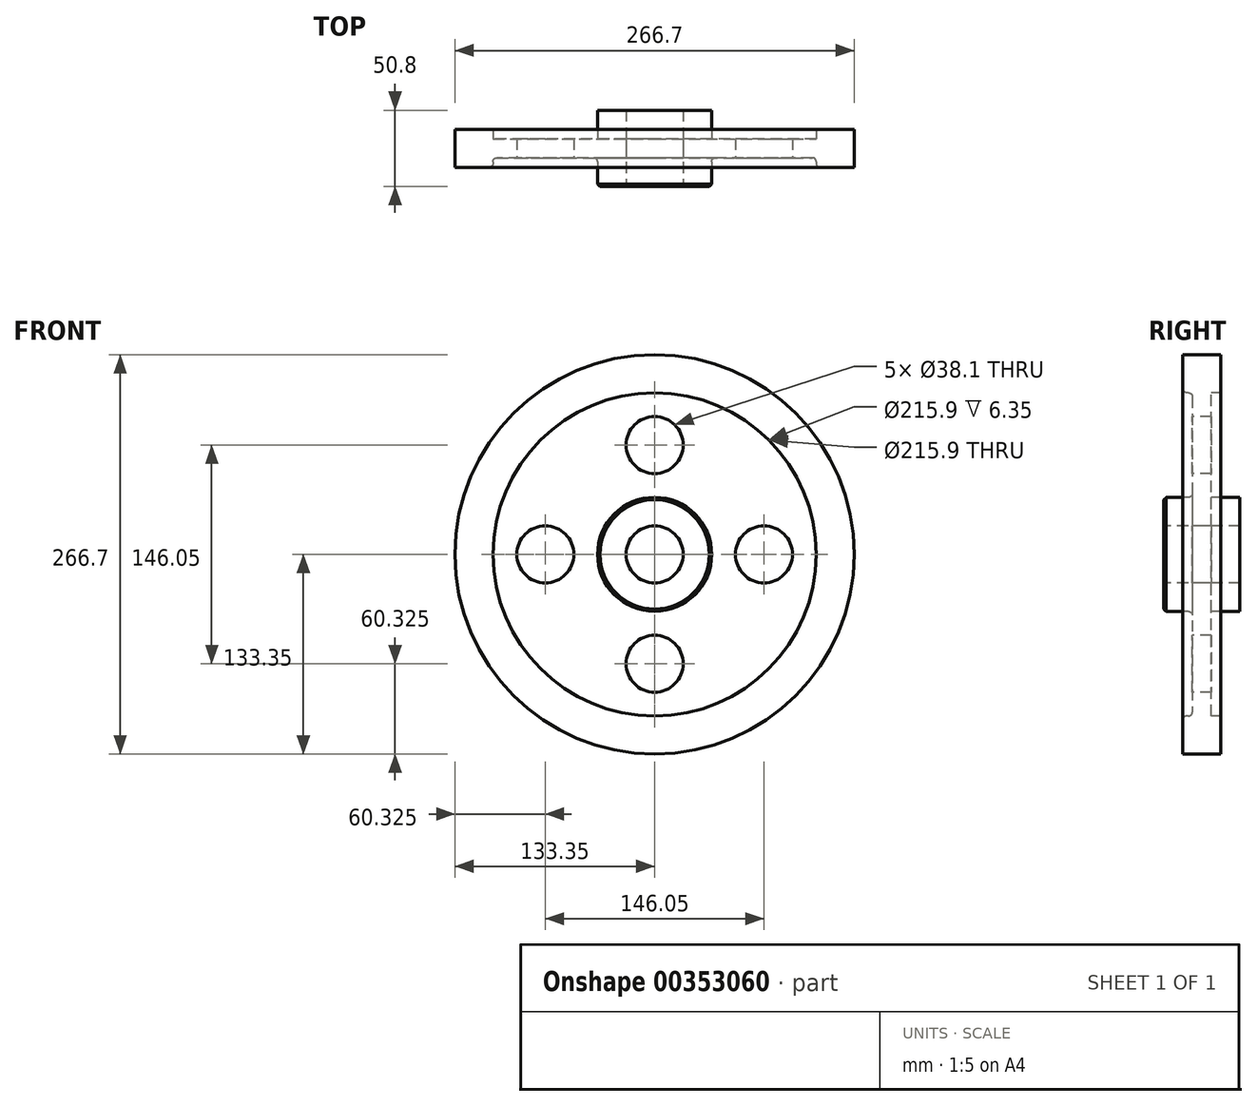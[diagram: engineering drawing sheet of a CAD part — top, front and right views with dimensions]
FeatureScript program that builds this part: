
annotation { "Feature Type Name" : "Feature", "Feature Type Description" : "" }
export const myFeature = defineFeature(function(context is Context, id is Id, definition is map)
    precondition{}
    {
        {
            var Q0;
            Q0=qCreatedBy(makeId("Right.planeOp"),FACE);
            var sketch = newSketch(context, id + "F0", { "sketchPlane" : qUnion([Q0])});
            skLineSegment(sketch, "E0", {"start": v(0, 0) * mm, "end": v(75.6, 0) * mm, "construction": true});
            skLineSegment(sketch, "E1.0", {"start": v(0, -2432.05) * mm, "end": v(75.6, -2432.05) * mm, "construction": true});
            skLineSegment(sketch, "E2.0", {"start": v(6.35, 107.95) * mm, "end": v(12.7, 107.95) * mm});
            skLineSegment(sketch, "E3", {"start": v(0, 133.35) * mm, "end": v(0, 0) * mm, "construction": true});
            skLineSegment(sketch, "E4.0", {"start": v(12.7, 133.35) * mm, "end": v(12.7, 107.95) * mm});
            skLineSegment(sketch, "E5.0", {"start": v(6.35, 107.95) * mm, "end": v(6.35, 38.1) * mm});
            skLineSegment(sketch, "E6", {"start": v(0, 133.35) * mm, "end": v(12.7, 133.35) * mm});
            skLineSegment(sketch, "E7.0", {"start": v(0, 317.5) * mm, "end": v(75.6, 317.5) * mm});
            skLineSegment(sketch, "E8.0", {"start": v(0, 38.1) * mm, "end": v(25.4, 38.1) * mm});
            skLineSegment(sketch, "E9.MirrorCS", {"start": v(0, 133.35) * mm, "end": v(-12.7, 133.35) * mm});
            skLineSegment(sketch, "E10.MirrorCS", {"start": v(-12.7, 133.35) * mm, "end": v(-12.7, 107.95) * mm});
            skLineSegment(sketch, "E11.MirrorCS", {"start": v(-6.35, 107.95) * mm, "end": v(-12.7, 107.95) * mm});
            skLineSegment(sketch, "E12.MirrorCS", {"start": v(-6.35, 107.95) * mm, "end": v(-6.35, 38.1) * mm});
            skLineSegment(sketch, "E13.MirrorCS", {"start": v(0, 38.1) * mm, "end": v(-25.4, 38.1) * mm});
            skLineSegment(sketch, "E14.0", {"start": v(0, 19.05) * mm, "end": v(75.6, 19.05) * mm});
            skLineSegment(sketch, "E15.bottom", {"start": v(-25.4, 38.1) * mm, "end": v(25.4, 38.1) * mm});
            skLineSegment(sketch, "E15.top", {"start": v(-25.4, 19.05) * mm, "end": v(25.4, 19.05) * mm});
            skLineSegment(sketch, "E15.left", {"start": v(-25.4, 38.1) * mm, "end": v(-25.4, 19.05) * mm});
            skLineSegment(sketch, "E15.right", {"start": v(25.4, 38.1) * mm, "end": v(25.4, 19.05) * mm});
            skPoint(sketch, "E16.MirrorCS.end.orphan", {"position": v(-25.4, 57.15) * mm});
            skPoint(sketch, "E16.MirrorCS.start.orphan", {"position": v(-6.35, 57.15) * mm});
            skPoint(sketch, "E17.trimOffspring.start.orphan", {"position": v(25.4, 57.15) * mm});
            skPoint(sketch, "E18.orphan", {"position": v(6.35, 57.15) * mm});
            skSolve(sketch);
        }
        {
            var Q0;
            Q0=makeQuery(id+"F0.imprint","IMPRINT",FACE,{"disambiguationData":[TD([[makeQuery(id+"F0.imprint","IMPRINT",EDGE,{"derivedFrom":sQuery(id+"F0.wireOp",EDGE,"E2.0")}),1.0]])]});
            var Q1;
            {var subQ2=sQuery(id+"F0.wireOp",EDGE,"E15.left");Q1=makeQuery(id+"F0.imprint","IMPRINT",FACE,{"disambiguationData":[TD([[makeQuery(id+"F0.imprint","IMPRINT",EDGE,{"derivedFrom":subQ2}),1.0]])]});}
            var Q2;
            Q2=sQuery(id+"F0.wireOp",EDGE,"E0");
            revolve(context, id + "F1", {"entities" : qUnion([Q0, Q1]), "axis" : qUnion([Q2]), "revolveType" : RevolveType.FULL});
        }
        {
            var Q0;
            Q0=makeQuery(id+"F1.opRevolve","SWEPT_FACE",FACE,{"disambiguationData":[OSD([sQuery(id+"F0.wireOp",EDGE,"E12.MirrorCS")])]});
            var sketch = newSketch(context, id + "F2", { "sketchPlane" : qUnion([Q0])});
            skLineSegment(sketch, "E19", {"start": v(0, 0) * mm, "end": v(0, 73.03) * mm});
            skCircle(sketch, "E20", {"center": v(0, 73.03) * mm, "radius": 19.05 * mm});
            skCircle(sketch, "E21.1.0", {"center": v(-73.03, 0) * mm, "radius": 19.05 * mm});
            skCircle(sketch, "E21.2.0", {"center": v(0, -73.03) * mm, "radius": 19.05 * mm});
            skCircle(sketch, "E21.3.0", {"center": v(73.03, 0) * mm, "radius": 19.05 * mm});
            skPoint(sketch, "E21.center", {"position": v(0, 0) * mm});
            skSolve(sketch);
        }
        {
            var Q0;
            {var subQ0=sQuery(id+"F2.wireOp",EDGE,"E21.3.0");var subQ1=makeQuery(id+"F1.opRevolve","SWEPT_EDGE",EDGE,{"disambiguationData":[OSD([sQuery(id+"F0.wireOp",EDGE,"E12.MirrorCS"),sQuery(id+"F0.wireOp",EDGE,"E16.MirrorCS")])]});var subQ2=makeQuery(id+"F2.imprint","INTERSECT",VERTEX,{"disambiguationData":[OD(0.0)],"derivedFrom":[subQ1,subQ0]});Q0=makeQuery(id+"F2.imprint","IMPRINT",FACE,{"disambiguationData":[TD([[makeQuery(id+"F2.imprint","IMPRINT",EDGE,{"disambiguationData":[TD([[subQ2,1.0]])],"derivedFrom":subQ0}),1.0]])]});}
            var Q1;
            {var subQ0=sQuery(id+"F2.wireOp",EDGE,"E21.2.0");var subQ1=makeQuery(id+"F1.opRevolve","SWEPT_EDGE",EDGE,{"disambiguationData":[OSD([sQuery(id+"F0.wireOp",EDGE,"E12.MirrorCS"),sQuery(id+"F0.wireOp",EDGE,"E16.MirrorCS")])]});var subQ2=makeQuery(id+"F2.imprint","INTERSECT",VERTEX,{"disambiguationData":[OD(0.0)],"derivedFrom":[subQ1,subQ0]});Q1=makeQuery(id+"F2.imprint","IMPRINT",FACE,{"disambiguationData":[TD([[makeQuery(id+"F2.imprint","IMPRINT",EDGE,{"disambiguationData":[TD([[subQ2,-1.0]])],"derivedFrom":subQ0}),1.0]])]});}
            var Q2;
            {var subQ0=sQuery(id+"F2.wireOp",EDGE,"E21.1.0");var subQ1=makeQuery(id+"F1.opRevolve","SWEPT_EDGE",EDGE,{"disambiguationData":[OSD([sQuery(id+"F0.wireOp",EDGE,"E12.MirrorCS"),sQuery(id+"F0.wireOp",EDGE,"E16.MirrorCS")])]});var subQ2=makeQuery(id+"F2.imprint","INTERSECT",VERTEX,{"disambiguationData":[OD(0.0)],"derivedFrom":[subQ1,subQ0]});Q2=makeQuery(id+"F2.imprint","IMPRINT",FACE,{"disambiguationData":[TD([[makeQuery(id+"F2.imprint","IMPRINT",EDGE,{"disambiguationData":[TD([[subQ2,-1.0]])],"derivedFrom":subQ0}),1.0]])]});}
            var Q3;
            {var subQ0=sQuery(id+"F2.wireOp",EDGE,"E20");var subQ1=makeQuery(id+"F1.opRevolve","SWEPT_EDGE",EDGE,{"disambiguationData":[OSD([sQuery(id+"F0.wireOp",EDGE,"E12.MirrorCS"),sQuery(id+"F0.wireOp",EDGE,"E16.MirrorCS")])]});var subQ2=makeQuery(id+"F2.imprint","INTERSECT",VERTEX,{"disambiguationData":[OD(0.0)],"derivedFrom":[subQ1,subQ0]});Q3=makeQuery(id+"F2.imprint","IMPRINT",FACE,{"disambiguationData":[TD([[makeQuery(id+"F2.imprint","IMPRINT",EDGE,{"disambiguationData":[TD([[subQ2,1.0]])],"derivedFrom":subQ0}),1.0]])]});}
            var Q4;
            Q4=makeQuery(id+"F2.imprint","IMPRINT",FACE,{"disambiguationData":[TD([[makeQuery(id+"F2.imprint","IMPRINT",EDGE,{"derivedFrom":sQuery(id+"F2.wireOp",EDGE,"E21.1.0")}),1.0]])]});
            var Q5;
            Q5=makeQuery(id+"F2.imprint","IMPRINT",FACE,{"disambiguationData":[TD([[makeQuery(id+"F2.imprint","IMPRINT",EDGE,{"derivedFrom":sQuery(id+"F2.wireOp",EDGE,"E21.3.0")}),1.0]])]});
            var Q6;
            Q6=makeQuery(id+"F2.imprint","IMPRINT",FACE,{"disambiguationData":[TD([[makeQuery(id+"F2.imprint","IMPRINT",EDGE,{"derivedFrom":sQuery(id+"F2.wireOp",EDGE,"E20")}),1.0]])]});
            var Q7;
            Q7=makeQuery(id+"F2.imprint","IMPRINT",FACE,{"disambiguationData":[TD([[makeQuery(id+"F2.imprint","IMPRINT",EDGE,{"derivedFrom":sQuery(id+"F2.wireOp",EDGE,"E21.2.0")}),1.0]])]});
            extrude(context, id + "F3", {"entities" : qUnion([Q0, Q1, Q2, Q3, Q4, Q5, Q6, Q7]), "operationType" : NewBodyOperationType.REMOVE, "oppositeDirection" : true, "depth" : 25.4 * mm});
        }
        {
            var Q0;
            {var subQ0=sQuery(id+"F2.wireOp",EDGE,"E20");var subQ1=sQuery(id+"F0.wireOp",EDGE,"E12.MirrorCS");var subQ2=sQuery(id+"F0.wireOp",EDGE,"E16.MirrorCS");var subQ3=sQuery(id+"F2.wireOp",EDGE,"E21.3.0");var subQ4=makeQuery(id+"F1.opRevolve","SWEPT_EDGE",EDGE,{"disambiguationData":[OSD([subQ1,subQ2])]});var subQ5=makeQuery(id+"F2.imprint","INTERSECT",VERTEX,{"derivedFrom":[subQ4,sQuery(id+"F2.wireOp",EDGE,"E19")]});var subQ6=sQuery(id+"F2.wireOp",EDGE,"E21.1.0");var subQ7=sQuery(id+"F2.wireOp",EDGE,"E21.2.0");Q0=makeQuery(id+"F3.boolean.opBoolean","SPLIT",EDGE,{"disambiguationData":[TD([makeQuery(id+"F1.opRevolve","SWEPT_FACE",FACE,{"disambiguationData":[OSD([sQuery(id+"F0.wireOp",EDGE,"4109ed80-6467-4f52-9944-9ac0837b3c0b.0")])]}),makeQuery(id+"F1.opRevolve","SWEPT_FACE",FACE,{"disambiguationData":[OSD([subQ1])]}),makeQuery(id+"F1.opRevolve","SWEPT_FACE",FACE,{"disambiguationData":[OSD([subQ2])]}),makeQuery(id+"F3.opExtrude","SWEPT_FACE",FACE,{"disambiguationData":[OSD([subQ0])]}),makeQuery(id+"F3.opExtrude","SWEPT_FACE",FACE,{"disambiguationData":[OSD([subQ3])]}),makeQuery(id+"F3.opExtrude","SWEPT_FACE",FACE,{"disambiguationData":[OSD([subQ1,subQ2]),TDD([makeQuery(id+"F2.imprint","IMPRINT",EDGE,{"disambiguationData":[TD([[subQ5,-1.0]])],"derivedFrom":subQ4}),makeQuery(id+"F2.imprint","IMPRINT",EDGE,{"disambiguationData":[TD([[subQ5,1.0]])],"derivedFrom":subQ4})])]}),makeQuery(id+"F3.opExtrude","SWEPT_FACE",FACE,{"disambiguationData":[OSD([subQ1,subQ2]),TDD([makeQuery(id+"F2.imprint","IMPRINT",EDGE,{"disambiguationData":[TD([[makeQuery(id+"F2.imprint","INTERSECT",VERTEX,{"disambiguationData":[OD(0.0)],"derivedFrom":[subQ4,subQ6]}),-1.0]])],"derivedFrom":subQ4})])]}),makeQuery(id+"F3.opExtrude","SWEPT_FACE",FACE,{"disambiguationData":[OSD([subQ1,subQ2]),TDD([makeQuery(id+"F2.imprint","IMPRINT",EDGE,{"disambiguationData":[TD([[makeQuery(id+"F2.imprint","INTERSECT",VERTEX,{"disambiguationData":[OD(0.0)],"derivedFrom":[subQ4,subQ7]}),-1.0]])],"derivedFrom":subQ4})])]}),makeQuery(id+"F3.opExtrude","SWEPT_FACE",FACE,{"disambiguationData":[OSD([subQ1,subQ2]),TDD([makeQuery(id+"F2.imprint","IMPRINT",EDGE,{"disambiguationData":[TD([[makeQuery(id+"F2.imprint","INTERSECT",VERTEX,{"disambiguationData":[OD(0.0)],"derivedFrom":[subQ4,subQ3]}),1.0]])],"derivedFrom":subQ4})])]})])],"derivedFrom":subQ4});}
            var Q1;
            {var subQ0=sQuery(id+"F2.wireOp",EDGE,"E20");var subQ1=sQuery(id+"F0.wireOp",EDGE,"E12.MirrorCS");var subQ2=sQuery(id+"F0.wireOp",EDGE,"E16.MirrorCS");var subQ3=sQuery(id+"F2.wireOp",EDGE,"E21.1.0");var subQ4=sQuery(id+"F2.wireOp",EDGE,"E21.2.0");var subQ5=makeQuery(id+"F1.opRevolve","SWEPT_EDGE",EDGE,{"disambiguationData":[OSD([subQ1,subQ2])]});var subQ6=makeQuery(id+"F2.imprint","INTERSECT",VERTEX,{"derivedFrom":[subQ5,sQuery(id+"F2.wireOp",EDGE,"E19")]});var subQ7=sQuery(id+"F2.wireOp",EDGE,"E21.3.0");Q1=makeQuery(id+"F3.boolean.opBoolean","SPLIT",EDGE,{"disambiguationData":[TD([makeQuery(id+"F1.opRevolve","SWEPT_FACE",FACE,{"disambiguationData":[OSD([sQuery(id+"F0.wireOp",EDGE,"4109ed80-6467-4f52-9944-9ac0837b3c0b.0")])]}),makeQuery(id+"F1.opRevolve","SWEPT_FACE",FACE,{"disambiguationData":[OSD([subQ1])]}),makeQuery(id+"F1.opRevolve","SWEPT_FACE",FACE,{"disambiguationData":[OSD([subQ2])]}),makeQuery(id+"F3.opExtrude","SWEPT_FACE",FACE,{"disambiguationData":[OSD([subQ0])]}),makeQuery(id+"F3.opExtrude","SWEPT_FACE",FACE,{"disambiguationData":[OSD([subQ3])]}),makeQuery(id+"F3.opExtrude","SWEPT_FACE",FACE,{"disambiguationData":[OSD([subQ1,subQ2]),TDD([makeQuery(id+"F2.imprint","IMPRINT",EDGE,{"disambiguationData":[TD([[subQ6,-1.0]])],"derivedFrom":subQ5}),makeQuery(id+"F2.imprint","IMPRINT",EDGE,{"disambiguationData":[TD([[subQ6,1.0]])],"derivedFrom":subQ5})])]}),makeQuery(id+"F3.opExtrude","SWEPT_FACE",FACE,{"disambiguationData":[OSD([subQ1,subQ2]),TDD([makeQuery(id+"F2.imprint","IMPRINT",EDGE,{"disambiguationData":[TD([[makeQuery(id+"F2.imprint","INTERSECT",VERTEX,{"disambiguationData":[OD(0.0)],"derivedFrom":[subQ5,subQ3]}),-1.0]])],"derivedFrom":subQ5})])]}),makeQuery(id+"F3.opExtrude","SWEPT_FACE",FACE,{"disambiguationData":[OSD([subQ1,subQ2]),TDD([makeQuery(id+"F2.imprint","IMPRINT",EDGE,{"disambiguationData":[TD([[makeQuery(id+"F2.imprint","INTERSECT",VERTEX,{"disambiguationData":[OD(0.0)],"derivedFrom":[subQ5,subQ4]}),-1.0]])],"derivedFrom":subQ5})])]}),makeQuery(id+"F3.opExtrude","SWEPT_FACE",FACE,{"disambiguationData":[OSD([subQ1,subQ2]),TDD([makeQuery(id+"F2.imprint","IMPRINT",EDGE,{"disambiguationData":[TD([[makeQuery(id+"F2.imprint","INTERSECT",VERTEX,{"disambiguationData":[OD(0.0)],"derivedFrom":[subQ5,subQ7]}),1.0]])],"derivedFrom":subQ5})])]})])],"derivedFrom":subQ5});}
            var Q2;
            {var subQ0=sQuery(id+"F2.wireOp",EDGE,"E21.2.0");var subQ1=sQuery(id+"F0.wireOp",EDGE,"E12.MirrorCS");var subQ2=sQuery(id+"F0.wireOp",EDGE,"E16.MirrorCS");var subQ3=sQuery(id+"F2.wireOp",EDGE,"E21.3.0");var subQ4=makeQuery(id+"F1.opRevolve","SWEPT_EDGE",EDGE,{"disambiguationData":[OSD([subQ1,subQ2])]});var subQ5=makeQuery(id+"F2.imprint","INTERSECT",VERTEX,{"derivedFrom":[subQ4,sQuery(id+"F2.wireOp",EDGE,"E19")]});var subQ7=sQuery(id+"F2.wireOp",EDGE,"E21.1.0");Q2=makeQuery(id+"F3.boolean.opBoolean","SPLIT",EDGE,{"disambiguationData":[TD([makeQuery(id+"F1.opRevolve","SWEPT_FACE",FACE,{"disambiguationData":[OSD([sQuery(id+"F0.wireOp",EDGE,"4109ed80-6467-4f52-9944-9ac0837b3c0b.0")])]}),makeQuery(id+"F1.opRevolve","SWEPT_FACE",FACE,{"disambiguationData":[OSD([subQ1])]}),makeQuery(id+"F1.opRevolve","SWEPT_FACE",FACE,{"disambiguationData":[OSD([subQ2])]}),makeQuery(id+"F3.opExtrude","SWEPT_FACE",FACE,{"disambiguationData":[OSD([subQ0])]}),makeQuery(id+"F3.opExtrude","SWEPT_FACE",FACE,{"disambiguationData":[OSD([subQ3])]}),makeQuery(id+"F3.opExtrude","SWEPT_FACE",FACE,{"disambiguationData":[OSD([subQ1,subQ2]),TDD([makeQuery(id+"F2.imprint","IMPRINT",EDGE,{"disambiguationData":[TD([[subQ5,-1.0]])],"derivedFrom":subQ4}),makeQuery(id+"F2.imprint","IMPRINT",EDGE,{"disambiguationData":[TD([[subQ5,1.0]])],"derivedFrom":subQ4})])]}),makeQuery(id+"F3.opExtrude","SWEPT_FACE",FACE,{"disambiguationData":[OSD([subQ1,subQ2]),TDD([makeQuery(id+"F2.imprint","IMPRINT",EDGE,{"disambiguationData":[TD([[makeQuery(id+"F2.imprint","INTERSECT",VERTEX,{"disambiguationData":[OD(0.0)],"derivedFrom":[subQ4,subQ7]}),-1.0]])],"derivedFrom":subQ4})])]}),makeQuery(id+"F3.opExtrude","SWEPT_FACE",FACE,{"disambiguationData":[OSD([subQ1,subQ2]),TDD([makeQuery(id+"F2.imprint","IMPRINT",EDGE,{"disambiguationData":[TD([[makeQuery(id+"F2.imprint","INTERSECT",VERTEX,{"disambiguationData":[OD(0.0)],"derivedFrom":[subQ4,subQ0]}),-1.0]])],"derivedFrom":subQ4})])]}),makeQuery(id+"F3.opExtrude","SWEPT_FACE",FACE,{"disambiguationData":[OSD([subQ1,subQ2]),TDD([makeQuery(id+"F2.imprint","IMPRINT",EDGE,{"disambiguationData":[TD([[makeQuery(id+"F2.imprint","INTERSECT",VERTEX,{"disambiguationData":[OD(0.0)],"derivedFrom":[subQ4,subQ3]}),1.0]])],"derivedFrom":subQ4})])]})])],"derivedFrom":subQ4});}
            var Q3;
            {var subQ0=sQuery(id+"F2.wireOp",EDGE,"E21.1.0");var subQ1=sQuery(id+"F2.wireOp",EDGE,"E21.2.0");var subQ2=sQuery(id+"F0.wireOp",EDGE,"E16.MirrorCS");var subQ3=sQuery(id+"F0.wireOp",EDGE,"E12.MirrorCS");var subQ4=makeQuery(id+"F1.opRevolve","SWEPT_EDGE",EDGE,{"disambiguationData":[OSD([subQ3,subQ2])]});var subQ5=makeQuery(id+"F2.imprint","INTERSECT",VERTEX,{"derivedFrom":[subQ4,sQuery(id+"F2.wireOp",EDGE,"E19")]});var subQ7=sQuery(id+"F2.wireOp",EDGE,"E21.3.0");Q3=makeQuery(id+"F3.boolean.opBoolean","SPLIT",EDGE,{"disambiguationData":[TD([makeQuery(id+"F1.opRevolve","SWEPT_FACE",FACE,{"disambiguationData":[OSD([sQuery(id+"F0.wireOp",EDGE,"4109ed80-6467-4f52-9944-9ac0837b3c0b.0")])]}),makeQuery(id+"F1.opRevolve","SWEPT_FACE",FACE,{"disambiguationData":[OSD([subQ3])]}),makeQuery(id+"F1.opRevolve","SWEPT_FACE",FACE,{"disambiguationData":[OSD([subQ2])]}),makeQuery(id+"F3.opExtrude","SWEPT_FACE",FACE,{"disambiguationData":[OSD([subQ0])]}),makeQuery(id+"F3.opExtrude","SWEPT_FACE",FACE,{"disambiguationData":[OSD([subQ1])]}),makeQuery(id+"F3.opExtrude","SWEPT_FACE",FACE,{"disambiguationData":[OSD([subQ3,subQ2]),TDD([makeQuery(id+"F2.imprint","IMPRINT",EDGE,{"disambiguationData":[TD([[subQ5,-1.0]])],"derivedFrom":subQ4}),makeQuery(id+"F2.imprint","IMPRINT",EDGE,{"disambiguationData":[TD([[subQ5,1.0]])],"derivedFrom":subQ4})])]}),makeQuery(id+"F3.opExtrude","SWEPT_FACE",FACE,{"disambiguationData":[OSD([subQ3,subQ2]),TDD([makeQuery(id+"F2.imprint","IMPRINT",EDGE,{"disambiguationData":[TD([[makeQuery(id+"F2.imprint","INTERSECT",VERTEX,{"disambiguationData":[OD(0.0)],"derivedFrom":[subQ4,subQ0]}),-1.0]])],"derivedFrom":subQ4})])]}),makeQuery(id+"F3.opExtrude","SWEPT_FACE",FACE,{"disambiguationData":[OSD([subQ3,subQ2]),TDD([makeQuery(id+"F2.imprint","IMPRINT",EDGE,{"disambiguationData":[TD([[makeQuery(id+"F2.imprint","INTERSECT",VERTEX,{"disambiguationData":[OD(0.0)],"derivedFrom":[subQ4,subQ1]}),-1.0]])],"derivedFrom":subQ4})])]}),makeQuery(id+"F3.opExtrude","SWEPT_FACE",FACE,{"disambiguationData":[OSD([subQ3,subQ2]),TDD([makeQuery(id+"F2.imprint","IMPRINT",EDGE,{"disambiguationData":[TD([[makeQuery(id+"F2.imprint","INTERSECT",VERTEX,{"disambiguationData":[OD(0.0)],"derivedFrom":[subQ4,subQ7]}),1.0]])],"derivedFrom":subQ4})])]})])],"derivedFrom":subQ4});}
            var Q4;
            Q4=makeQuery(id+"F1.opRevolve","SWEPT_EDGE",EDGE,{"disambiguationData":[OSD([sQuery(id+"F0.wireOp",EDGE,"E16.MirrorCS"),sQuery(id+"F0.wireOp",EDGE,"b710a490-952e-46a2-99dd-4c791f0e04cd0.MirrorCS")])]});
            var Q5;
            Q5=makeQuery(id+"F1.opRevolve","SWEPT_EDGE",EDGE,{"disambiguationData":[OSD([sQuery(id+"F0.wireOp",EDGE,"E11.MirrorCS"),sQuery(id+"F0.wireOp",EDGE,"E12.MirrorCS")])]});
            var Q6;
            Q6=makeQuery(id+"F1.opRevolve","SWEPT_EDGE",EDGE,{"disambiguationData":[OSD([sQuery(id+"F0.wireOp",EDGE,"E10.MirrorCS"),sQuery(id+"F0.wireOp",EDGE,"E11.MirrorCS")])]});
            fillet(context, id + "F4", {"entities" : qUnion([Q0, Q1, Q2, Q3, Q4, Q5, Q6]), "radius" : 2.54 * mm, "tangentPropagation" : true, "allowEdgeOverflow" : false});
        }
        {
            var Q0;
            Q0=makeQuery(id+"F1.opRevolve","SWEPT_EDGE",EDGE,{"disambiguationData":[OSD([sQuery(id+"F0.wireOp",EDGE,"b710a490-952e-46a2-99dd-4c791f0e04cd0.MirrorCS"),sQuery(id+"F0.wireOp",EDGE,"E13.MirrorCS")])]});
            chamfer(context, id + "F5", {"entities" : qUnion([Q0]), "width" : 1.59 * mm, "tangentPropagation" : true});
        }
    });
